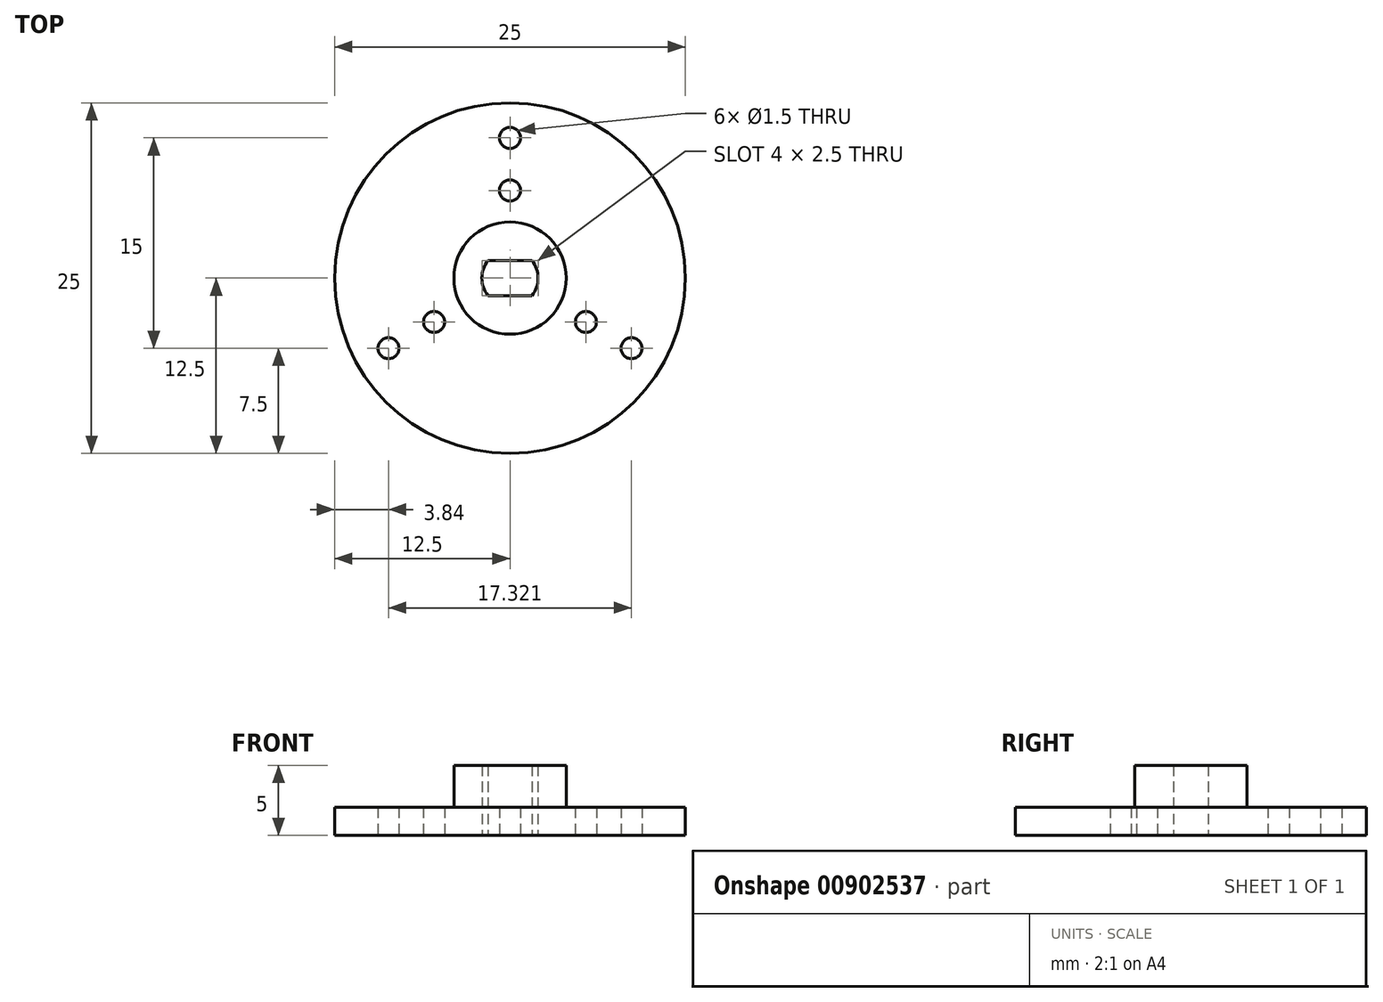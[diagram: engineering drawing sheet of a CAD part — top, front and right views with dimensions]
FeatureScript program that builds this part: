
annotation { "Feature Type Name" : "Feature", "Feature Type Description" : "" }
export const myFeature = defineFeature(function(context is Context, id is Id, definition is map)
    precondition{}
    {
        {
            var Q0;
            Q0=qCreatedBy(makeId("Top.planeOp"),FACE);
            var sketch = newSketch(context, id + "F0", { "sketchPlane" : qUnion([Q0])});
            skCircle(sketch, "E0", {"center": v(0, 0) * mm, "radius": 2 * mm});
            skCircle(sketch, "E1", {"center": v(0, 0) * mm, "radius": 4 * mm});
            skLineSegment(sketch, "E2.bottom", {"start": v(-1.56, 1.25) * mm, "end": v(1.56, 1.25) * mm});
            skLineSegment(sketch, "E2.top", {"start": v(-1.56, -1.25) * mm, "end": v(1.56, -1.25) * mm});
            skLineSegment(sketch, "E2.left", {"start": v(-1.56, 1.25) * mm, "end": v(-1.56, -1.25) * mm});
            skLineSegment(sketch, "E2.right", {"start": v(1.56, 1.25) * mm, "end": v(1.56, -1.25) * mm});
            skCircle(sketch, "E3", {"center": v(0, 0) * mm, "radius": 12.5 * mm});
            skLineSegment(sketch, "E4", {"start": v(0, 0) * mm, "end": v(0, 12.5) * mm});
            skCircle(sketch, "E5", {"center": v(0, 6.25) * mm, "radius": 0.75 * mm});
            skCircle(sketch, "E6", {"center": v(0, 10) * mm, "radius": 0.75 * mm});
            skCircle(sketch, "E7.1.0", {"center": v(-5.41, -3.12) * mm, "radius": 0.75 * mm});
            skCircle(sketch, "E7.1.1", {"center": v(-8.66, -5) * mm, "radius": 0.75 * mm});
            skCircle(sketch, "E7.2.0", {"center": v(5.41, -3.13) * mm, "radius": 0.75 * mm});
            skCircle(sketch, "E7.2.1", {"center": v(8.66, -5) * mm, "radius": 0.75 * mm});
            skSolve(sketch);
        }
        {
            var Q0;
            Q0=makeQuery(id+"F0.imprint","IMPRINT",FACE,{"disambiguationData":[TD([[makeQuery(id+"F0.imprint","IMPRINT",EDGE,{"derivedFrom":sQuery(id+"F0.wireOp",EDGE,"E1")}),-1.0]])]});
            extrude(context, id + "F1", {"entities" : qUnion([Q0]), "depth" : 2 * mm, "offsetDistance" : 25 * mm});
        }
        {
            var Q0;
            Q0=makeQuery(id+"F0.imprint","IMPRINT",FACE,{"disambiguationData":[TD([[makeQuery(id+"F0.imprint","IMPRINT",EDGE,{"derivedFrom":sQuery(id+"F0.wireOp",EDGE,"E1")}),1.0]])]});
            var Q1;
            {var subQ1=sQuery(id+"F0.wireOp",EDGE,"E0");var subQ3=sQuery(id+"F0.wireOp",EDGE,"E4");var subQ4=makeQuery(id+"F0.imprint","INTERSECT",VERTEX,{"derivedFrom":[subQ1,subQ3]});Q1=makeQuery(id+"F0.imprint","IMPRINT",FACE,{"disambiguationData":[TD([[makeQuery(id+"F0.imprint","IMPRINT",EDGE,{"disambiguationData":[TD([[subQ4,1.0]])],"derivedFrom":subQ3}),-1.0]])]});}
            var Q2;
            {var subQ1=sQuery(id+"F0.wireOp",EDGE,"E0");var subQ3=sQuery(id+"F0.wireOp",EDGE,"E4");var subQ4=makeQuery(id+"F0.imprint","INTERSECT",VERTEX,{"derivedFrom":[subQ1,subQ3]});Q2=makeQuery(id+"F0.imprint","IMPRINT",FACE,{"disambiguationData":[TD([[makeQuery(id+"F0.imprint","IMPRINT",EDGE,{"disambiguationData":[TD([[subQ4,1.0]])],"derivedFrom":subQ3}),1.0]])]});}
            var Q3;
            {var subQ0=sQuery(id+"F0.wireOp",EDGE,"E2.top");Q3=makeQuery(id+"F0.imprint","IMPRINT",FACE,{"disambiguationData":[TD([[makeQuery(id+"F0.imprint","IMPRINT",EDGE,{"derivedFrom":subQ0}),-1.0]])]});}
            extrude(context, id + "F2", {"entities" : qUnion([Q0, Q1, Q2, Q3]), "operationType" : NewBodyOperationType.ADD, "depth" : 5 * mm, "offsetDistance" : 25 * mm});
        }
    });
